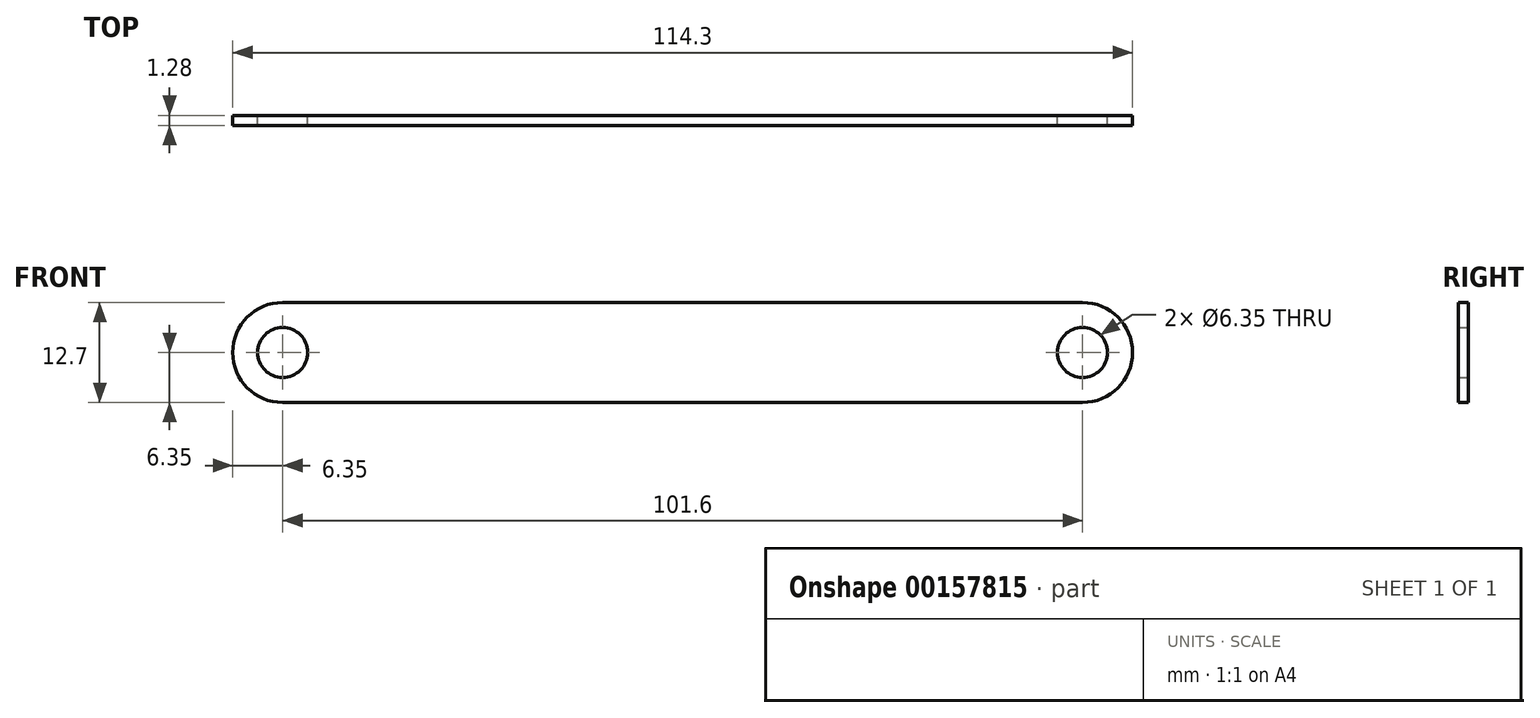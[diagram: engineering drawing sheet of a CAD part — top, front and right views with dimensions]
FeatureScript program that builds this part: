
annotation { "Feature Type Name" : "Feature", "Feature Type Description" : "" }
export const myFeature = defineFeature(function(context is Context, id is Id, definition is map)
    precondition{}
    {
        {
            var Q0;
            Q0=qCreatedBy(makeId("Front.planeOp"),FACE);
            var sketch = newSketch(context, id + "F0", { "sketchPlane" : qUnion([Q0])});
            skLineSegment(sketch, "E0.bottom", {"start": v(50.8, -6.35) * mm, "end": v(-50.8, -6.35) * mm});
            skLineSegment(sketch, "E0.top", {"start": v(50.8, 6.35) * mm, "end": v(-50.8, 6.35) * mm});
            skLineSegment(sketch, "E0.left", {"start": v(50.8, -6.35) * mm, "end": v(50.8, 6.35) * mm});
            skLineSegment(sketch, "E0.right", {"start": v(-50.8, -6.35) * mm, "end": v(-50.8, 6.35) * mm});
            skPoint(sketch, "E0.middle", {"position": v(0, 0) * mm});
            skArc(sketch, "E1", {"start": v(-50.8, 6.35) * mm, "mid": v(-57.15, 0) * mm, "end": v(-50.8, -6.35) * mm});
            skArc(sketch, "E2", {"start": v(-50.8, -6.35) * mm, "mid": v(-44.45, 0) * mm, "end": v(-50.8, 6.35) * mm, "construction": true});
            skArc(sketch, "E3", {"start": v(50.8, 6.35) * mm, "mid": v(44.45, 0) * mm, "end": v(50.8, -6.35) * mm, "construction": true});
            skArc(sketch, "E4", {"start": v(50.8, -6.35) * mm, "mid": v(57.15, 0) * mm, "end": v(50.8, 6.35) * mm});
            skCircle(sketch, "E5", {"center": v(-50.8, 0) * mm, "radius": 3.18 * mm});
            skCircle(sketch, "E6", {"center": v(50.8, 0) * mm, "radius": 3.18 * mm});
            skSolve(sketch);
        }
        {
            var Q0;
            Q0 = qSketchRegion(id + "F0", true);
            extrude(context, id + "F1", {"entities" : qUnion([Q0]), "endBound" : BoundingType.SYMMETRIC, "depth" : 1.27 * mm});
        }
    });
